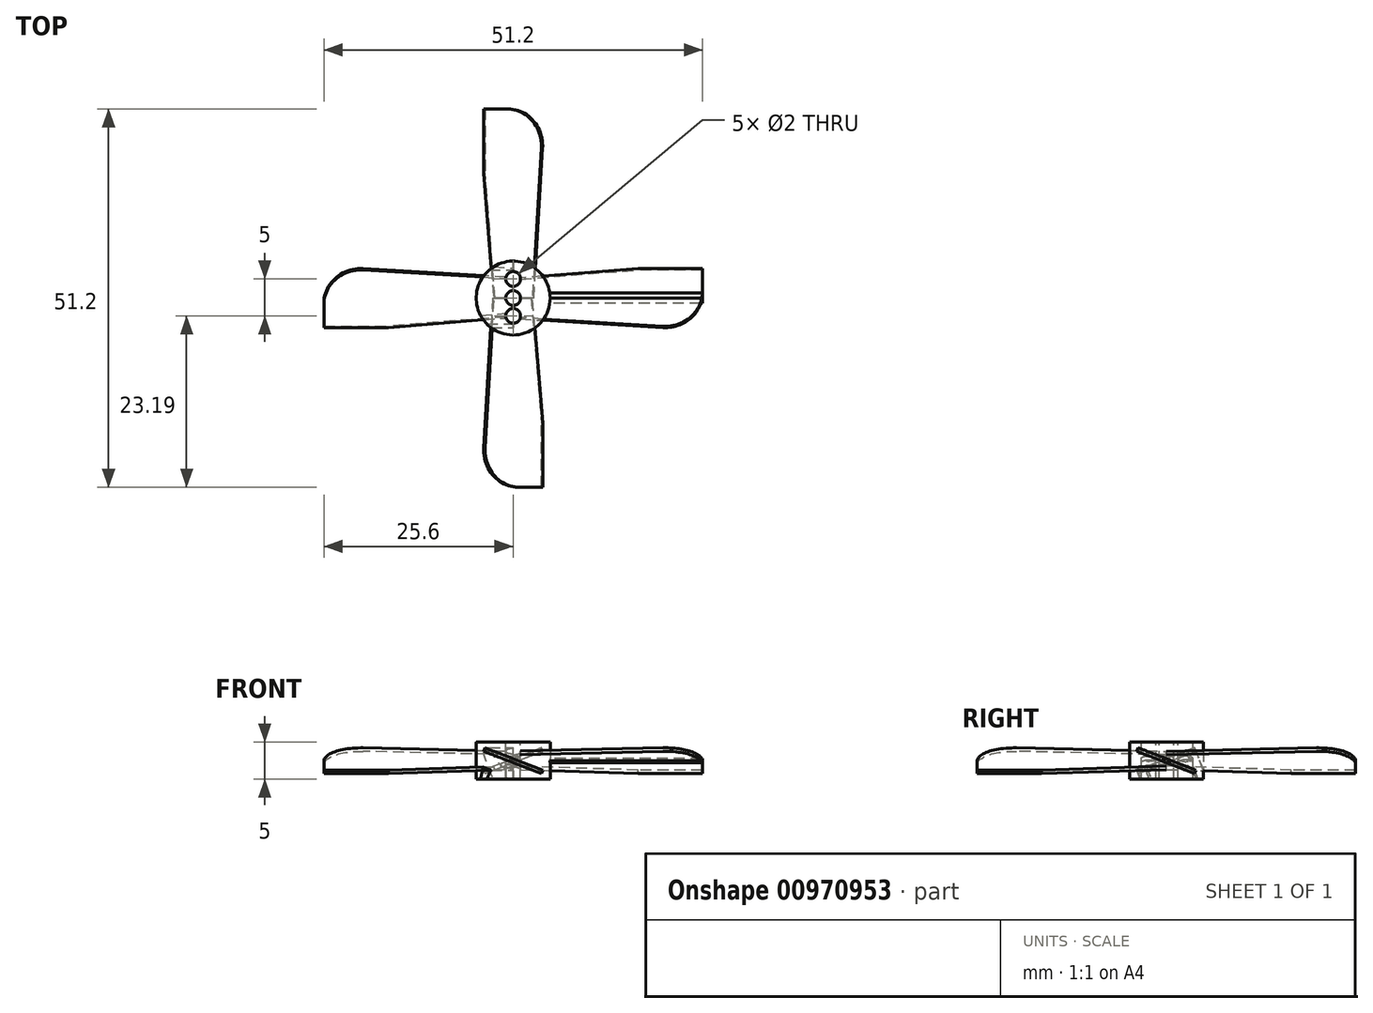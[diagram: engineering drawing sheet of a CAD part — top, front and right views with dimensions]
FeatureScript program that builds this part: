
annotation { "Feature Type Name" : "Feature", "Feature Type Description" : "" }
export const myFeature = defineFeature(function(context is Context, id is Id, definition is map)
    precondition{}
    {
        {
            var Q0;
            Q0=qCreatedBy(makeId("Top.planeOp"),FACE);
            var sketch = newSketch(context, id + "F0", { "sketchPlane" : qUnion([Q0])});
            skCircle(sketch, "E0", {"center": v(0, 0) * mm, "radius": 5 * mm});
            skSolve(sketch);
        }
        {
            var Q0;
            Q0=makeQuery(id+"F0.imprint","IMPRINT",FACE,{"disambiguationData":[TD([[makeQuery(id+"F0.imprint","IMPRINT",EDGE,{"derivedFrom":sQuery(id+"F0.wireOp",EDGE,"E0")}),1.0]])]});
            extrude(context, id + "F1", {"entities" : qUnion([Q0]), "depth" : 5 * mm, "offsetDistance" : 25 * mm});
        }
        {
            var Q0;
            Q0=qCreatedBy(makeId("Right.planeOp"),FACE);
            var sketch = newSketch(context, id + "F2", { "sketchPlane" : qUnion([Q0])});
            skLineSegment(sketch, "E1", {"start": v(0, 0) * mm, "end": v(0, 6.66) * mm, "construction": true});
            skLineSegment(sketch, "E2", {"start": v(0, 0) * mm, "end": v(8.16, 0) * mm, "construction": true});
            skLineSegment(sketch, "E3", {"start": v(-3.9, 1) * mm, "end": v(3.9, 4) * mm, "construction": true});
            skLineSegment(sketch, "E4.0", {"start": v(-3.99, 1.23) * mm, "end": v(3.81, 4.23) * mm});
            skLineSegment(sketch, "E5.0", {"start": v(-3.81, 0.77) * mm, "end": v(3.99, 3.77) * mm});
            skLineSegment(sketch, "E6", {"start": v(3.81, 4.23) * mm, "end": v(3.99, 3.77) * mm});
            skLineSegment(sketch, "E7", {"start": v(-3.81, 0.77) * mm, "end": v(-3.99, 1.23) * mm});
            skPoint(sketch, "E8.visualSharp", {"position": v(3.81, 4.23) * mm});
            skPoint(sketch, "E9.visualSharp", {"position": v(3.99, 3.77) * mm});
            skPoint(sketch, "E10.visualSharp", {"position": v(-3.81, 0.77) * mm});
            skPoint(sketch, "E11.visualSharp", {"position": v(-3.99, 1.23) * mm});
            skLineSegment(sketch, "E12.MirrorCS", {"start": v(3.99, 1.23) * mm, "end": v(-3.81, 4.23) * mm});
            skLineSegment(sketch, "E13.MirrorCS", {"start": v(3.81, 0.77) * mm, "end": v(-3.99, 3.77) * mm});
            skLineSegment(sketch, "E14.MirrorCS", {"start": v(3.9, 1) * mm, "end": v(-3.9, 4) * mm, "construction": true});
            skLineSegment(sketch, "E15.MirrorCS", {"start": v(-3.81, 4.23) * mm, "end": v(-3.99, 3.77) * mm});
            skLineSegment(sketch, "E16.MirrorCS", {"start": v(3.81, 0.77) * mm, "end": v(3.99, 1.23) * mm});
            skSolve(sketch);
        }
        {
            var Q0;
            {var subQ0=sQuery(id+"F2.wireOp",EDGE,"9761674e-4ed2-4d5f-bec5-4fd517a730660.MirrorCS");Q0=makeQuery(id+"F2.imprint","IMPRINT",FACE,{"disambiguationData":[TD([[makeQuery(id+"F2.imprint","IMPRINT",EDGE,{"derivedFrom":subQ0}),-1.0]])]});}
            var Q1;
            {var subQ0=sQuery(id+"F2.wireOp",EDGE,"0e20b040-7c01-4561-af6c-762be206c4af0.MirrorCS");Q1=makeQuery(id+"F2.imprint","IMPRINT",FACE,{"disambiguationData":[TD([[makeQuery(id+"F2.imprint","IMPRINT",EDGE,{"derivedFrom":subQ0}),-1.0]])]});}
            var Q2;
            {var subQ0=sQuery(id+"F2.wireOp",EDGE,"E13.MirrorCS");var subQ1=sQuery(id+"F2.wireOp",EDGE,"E4.0");var subQ2=makeQuery(id+"F2.imprint","INTERSECT",VERTEX,{"derivedFrom":[subQ1,subQ0]});Q2=makeQuery(id+"F2.imprint","IMPRINT",FACE,{"disambiguationData":[TD([[makeQuery(id+"F2.imprint","IMPRINT",EDGE,{"disambiguationData":[TD([[subQ2,-1.0]])],"derivedFrom":subQ1}),-1.0]])]});}
            extrude(context, id + "F3", {"entities" : qUnion([Q0, Q1, Q2]), "operationType" : NewBodyOperationType.ADD, "depth" : 25.6 * mm, "offsetDistance" : 25 * mm});
        }
        {
            var Q0;
            Q0=makeQuery(id+"F2.imprint","IMPRINT",FACE,{"disambiguationData":[TD([[makeQuery(id+"F2.imprint","IMPRINT",EDGE,{"derivedFrom":sQuery(id+"F2.wireOp",EDGE,"E6")}),-1.0]])]});
            var Q1;
            Q1=makeQuery(id+"F2.imprint","IMPRINT",FACE,{"disambiguationData":[TD([[makeQuery(id+"F2.imprint","IMPRINT",EDGE,{"derivedFrom":sQuery(id+"F2.wireOp",EDGE,"E7")}),-1.0]])]});
            var Q2;
            {var subQ0=sQuery(id+"F2.wireOp",EDGE,"E13.MirrorCS");var subQ1=sQuery(id+"F2.wireOp",EDGE,"E4.0");var subQ2=makeQuery(id+"F2.imprint","INTERSECT",VERTEX,{"derivedFrom":[subQ1,subQ0]});Q2=makeQuery(id+"F2.imprint","IMPRINT",FACE,{"disambiguationData":[TD([[makeQuery(id+"F2.imprint","IMPRINT",EDGE,{"disambiguationData":[TD([[subQ2,-1.0]])],"derivedFrom":subQ1}),-1.0]])]});}
            extrude(context, id + "F4", {"entities" : qUnion([Q0, Q1, Q2]), "oppositeDirection" : true, "depth" : 25.6 * mm, "offsetDistance" : 25 * mm});
        }
        {
            var Q0;
            Q0=makeQuery(id+"F4.opExtrude","SWEPT_FACE",FACE,{"disambiguationData":[OSD([sQuery(id+"F2.wireOp",EDGE,"E4.0")])]});
            var sketch = newSketch(context, id + "F5", { "sketchPlane" : qUnion([Q0])});
            skCircle(sketch, "E17", {"center": v(-20.6, 0.08) * mm, "radius": 5 * mm});
            skLineSegment(sketch, "E18", {"start": v(-20.28, 5.07) * mm, "end": v(0, 3.78) * mm});
            skLineSegment(sketch, "E19", {"start": v(-16.9, -3.28) * mm, "end": v(0, -1.82) * mm});
            skSolve(sketch);
        }
        {
            var Q0;
            {var subQ0=sQuery(id+"F5.wireOp",EDGE,"E17");var subQ1=sQuery(id+"F2.wireOp",EDGE,"E4.0");var subQ2=makeQuery(id+"F4.opExtrude","CAP_EDGE",EDGE,{"disambiguationData":[OSD([subQ1])],"isStart":false});var subQ3=makeQuery(id+"F5.imprint","INTERSECT",VERTEX,{"derivedFrom":[subQ2,subQ0]});Q0=makeQuery(id+"F5.imprint","IMPRINT",FACE,{"disambiguationData":[TD([[makeQuery(id+"F5.imprint","IMPRINT",EDGE,{"disambiguationData":[TD([[subQ3,1.0]])],"derivedFrom":subQ0}),-1.0]])]});}
            var Q1;
            {var subQ0=sQuery(id+"F5.wireOp",EDGE,"E18");Q1=makeQuery(id+"F5.imprint","IMPRINT",FACE,{"disambiguationData":[TD([[makeQuery(id+"F5.imprint","IMPRINT",EDGE,{"derivedFrom":subQ0}),1.0]])]});}
            var Q2;
            {var subQ0=sQuery(id+"F5.wireOp",EDGE,"E19");Q2=makeQuery(id+"F5.imprint","IMPRINT",FACE,{"disambiguationData":[TD([[makeQuery(id+"F5.imprint","IMPRINT",EDGE,{"derivedFrom":subQ0}),-1.0]])]});}
            extrude(context, id + "F6", {"entities" : qUnion([Q0, Q1, Q2]), "operationType" : NewBodyOperationType.REMOVE, "oppositeDirection" : true, "depth" : 25 * mm, "offsetDistance" : 25 * mm});
        }
        {
            var Q0;
            Q0=makeQuery(id+"F4.opExtrude","SWEPT_BODY",BODY,{"disambiguationData":[OSD([sQuery(id+"F2.wireOp",EDGE,"E4.0"),sQuery(id+"F2.wireOp",EDGE,"E5.0"),sQuery(id+"F2.wireOp",EDGE,"E6"),sQuery(id+"F2.wireOp",EDGE,"E7"),sQuery(id+"F2.wireOp",EDGE,"E8.filletArc"),sQuery(id+"F2.wireOp",EDGE,"E9.filletArc"),sQuery(id+"F2.wireOp",EDGE,"E10.filletArc"),sQuery(id+"F2.wireOp",EDGE,"E11.filletArc")])]});
            var Q1;
            Q1=sQuery(id+"F2.wireOp",EDGE,"E1");
            circularPattern(context, id + "F7", {"entities" : qUnion([Q0]), "axis" : qUnion([Q1]), "angle" : 360 * degree, "instanceCount" : 4, "equalSpace" : true});
        }
        {
            var Q0;
            Q0=makeQuery(id+"F1.opExtrude","CAP_FACE",FACE,{"disambiguationData":[OSD([sQuery(id+"F0.wireOp",EDGE,"E0")])],"isStart":false});
            var sketch = newSketch(context, id + "F8", { "sketchPlane" : qUnion([Q0])});
            skCircle(sketch, "E20", {"center": v(0, 0) * mm, "radius": 1 * mm});
            skCircle(sketch, "E21", {"center": v(0, 2.59) * mm, "radius": 1 * mm});
            skCircle(sketch, "E22", {"center": v(0, -2.41) * mm, "radius": 1 * mm});
            skSolve(sketch);
        }
        {
            var Q0;
            Q0=makeQuery(id+"F8.imprint","IMPRINT",FACE,{"disambiguationData":[TD([[makeQuery(id+"F8.imprint","IMPRINT",EDGE,{"derivedFrom":sQuery(id+"F8.wireOp",EDGE,"E20")}),1.0]])]});
            var Q1;
            Q1=makeQuery(id+"F8.imprint","IMPRINT",FACE,{"disambiguationData":[TD([[makeQuery(id+"F8.imprint","IMPRINT",EDGE,{"derivedFrom":sQuery(id+"F8.wireOp",EDGE,"E21")}),1.0]])]});
            var Q2;
            Q2=makeQuery(id+"F8.imprint","IMPRINT",FACE,{"disambiguationData":[TD([[makeQuery(id+"F8.imprint","IMPRINT",EDGE,{"derivedFrom":sQuery(id+"F8.wireOp",EDGE,"E22")}),1.0]])]});
            extrude(context, id + "F9", {"entities" : qUnion([Q0, Q1, Q2]), "operationType" : NewBodyOperationType.REMOVE, "oppositeDirection" : true, "depth" : 25 * mm, "offsetDistance" : 25 * mm});
        }
    });
